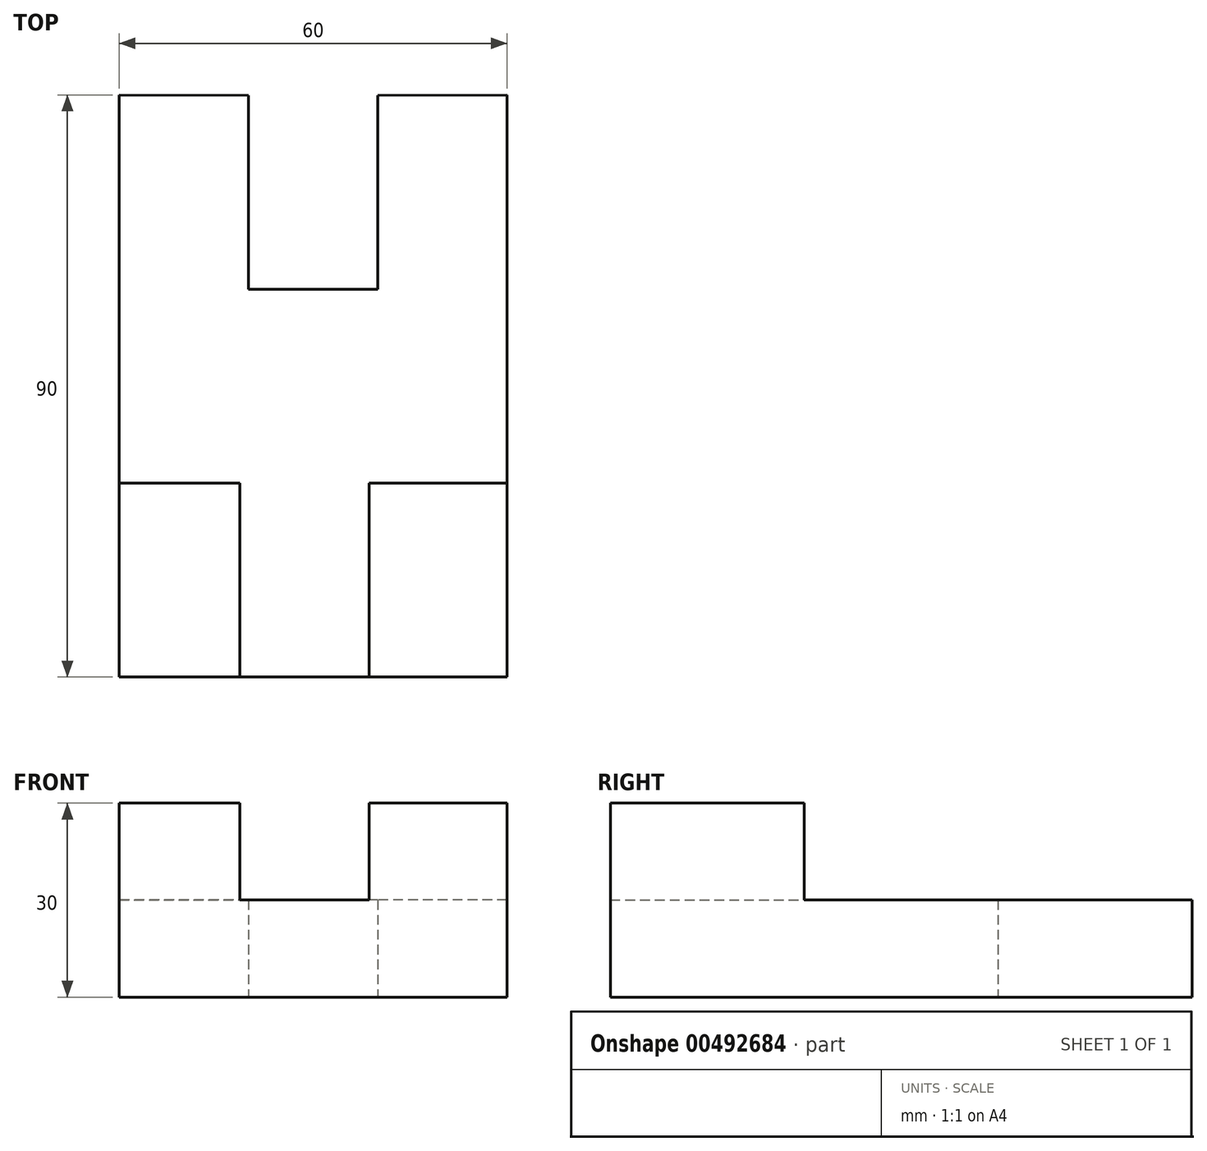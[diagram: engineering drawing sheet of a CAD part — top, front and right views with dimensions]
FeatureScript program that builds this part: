
annotation { "Feature Type Name" : "Feature", "Feature Type Description" : "" }
export const myFeature = defineFeature(function(context is Context, id is Id, definition is map)
    precondition{}
    {
        {
            var Q0;
            Q0=qCreatedBy(makeId("Top.planeOp"),FACE);
            var sketch = newSketch(context, id + "F0", { "sketchPlane" : qUnion([Q0])});
            skLineSegment(sketch, "E0.top", {"start": v(-46.23, -46) * mm, "end": v(13.77, -46) * mm});
            skLineSegment(sketch, "E0.left", {"start": v(-46.23, 44) * mm, "end": v(-46.23, -46) * mm});
            skLineSegment(sketch, "E0.right", {"start": v(13.77, 44) * mm, "end": v(13.77, -46) * mm});
            skLineSegment(sketch, "E1.bottom", {"start": v(-6.23, 13.96) * mm, "end": v(-26.23, 13.96) * mm});
            skLineSegment(sketch, "E1.left", {"start": v(-6.23, 13.96) * mm, "end": v(-6.23, 43.96) * mm});
            skLineSegment(sketch, "E1.right", {"start": v(-26.23, 13.96) * mm, "end": v(-26.23, 43.96) * mm});
            skLineSegment(sketch, "E2", {"start": v(13.77, 44) * mm, "end": v(-6.23, 43.96) * mm});
            skLineSegment(sketch, "E3", {"start": v(-26.23, 43.96) * mm, "end": v(-46.23, 44) * mm});
            skSolve(sketch);
        }
        {
            var Q0;
            Q0=makeQuery(id+"F0.imprint","IMPRINT",FACE,{"disambiguationData":[TD([[makeQuery(id+"F0.imprint","IMPRINT",EDGE,{"derivedFrom":sQuery(id+"F0.wireOp",EDGE,"E0.top")}),1.0]])]});
            extrude(context, id + "F1", {"entities" : qUnion([Q0]), "depth" : 15 * mm});
        }
        {
            var Q0;
            Q0=makeQuery(id+"F1.opExtrude","CAP_FACE",FACE,{"disambiguationData":[OSD([sQuery(id+"F0.wireOp",EDGE,"E0.top"),sQuery(id+"F0.wireOp",EDGE,"E0.left"),sQuery(id+"F0.wireOp",EDGE,"E0.right"),sQuery(id+"F0.wireOp",EDGE,"E1.bottom"),sQuery(id+"F0.wireOp",EDGE,"E1.left"),sQuery(id+"F0.wireOp",EDGE,"E1.right"),sQuery(id+"F0.wireOp",EDGE,"E2"),sQuery(id+"F0.wireOp",EDGE,"E3")])],"isStart":false});
            var sketch = newSketch(context, id + "F2", { "sketchPlane" : qUnion([Q0])});
            skLineSegment(sketch, "E4.bottom", {"start": v(-46.23, -46) * mm, "end": v(-27.58, -46) * mm});
            skLineSegment(sketch, "E4.top", {"start": v(-46.23, -16) * mm, "end": v(-27.58, -16) * mm});
            skLineSegment(sketch, "E4.left", {"start": v(-46.23, -46) * mm, "end": v(-46.23, -16) * mm});
            skLineSegment(sketch, "E4.right", {"start": v(-27.58, -46) * mm, "end": v(-27.58, -16) * mm});
            skLineSegment(sketch, "E5.bottom", {"start": v(13.77, -46) * mm, "end": v(-7.58, -46) * mm});
            skLineSegment(sketch, "E5.top", {"start": v(13.77, -16) * mm, "end": v(-7.58, -16) * mm});
            skLineSegment(sketch, "E5.left", {"start": v(13.77, -46) * mm, "end": v(13.77, -16) * mm});
            skLineSegment(sketch, "E5.right", {"start": v(-7.58, -46) * mm, "end": v(-7.58, -16) * mm});
            skSolve(sketch);
        }
        {
            var Q0;
            Q0 = qSketchRegion(id + "F2", true);
            extrude(context, id + "F3", {"entities" : qUnion([Q0]), "operationType" : NewBodyOperationType.ADD, "depth" : 15 * mm});
        }
    });
